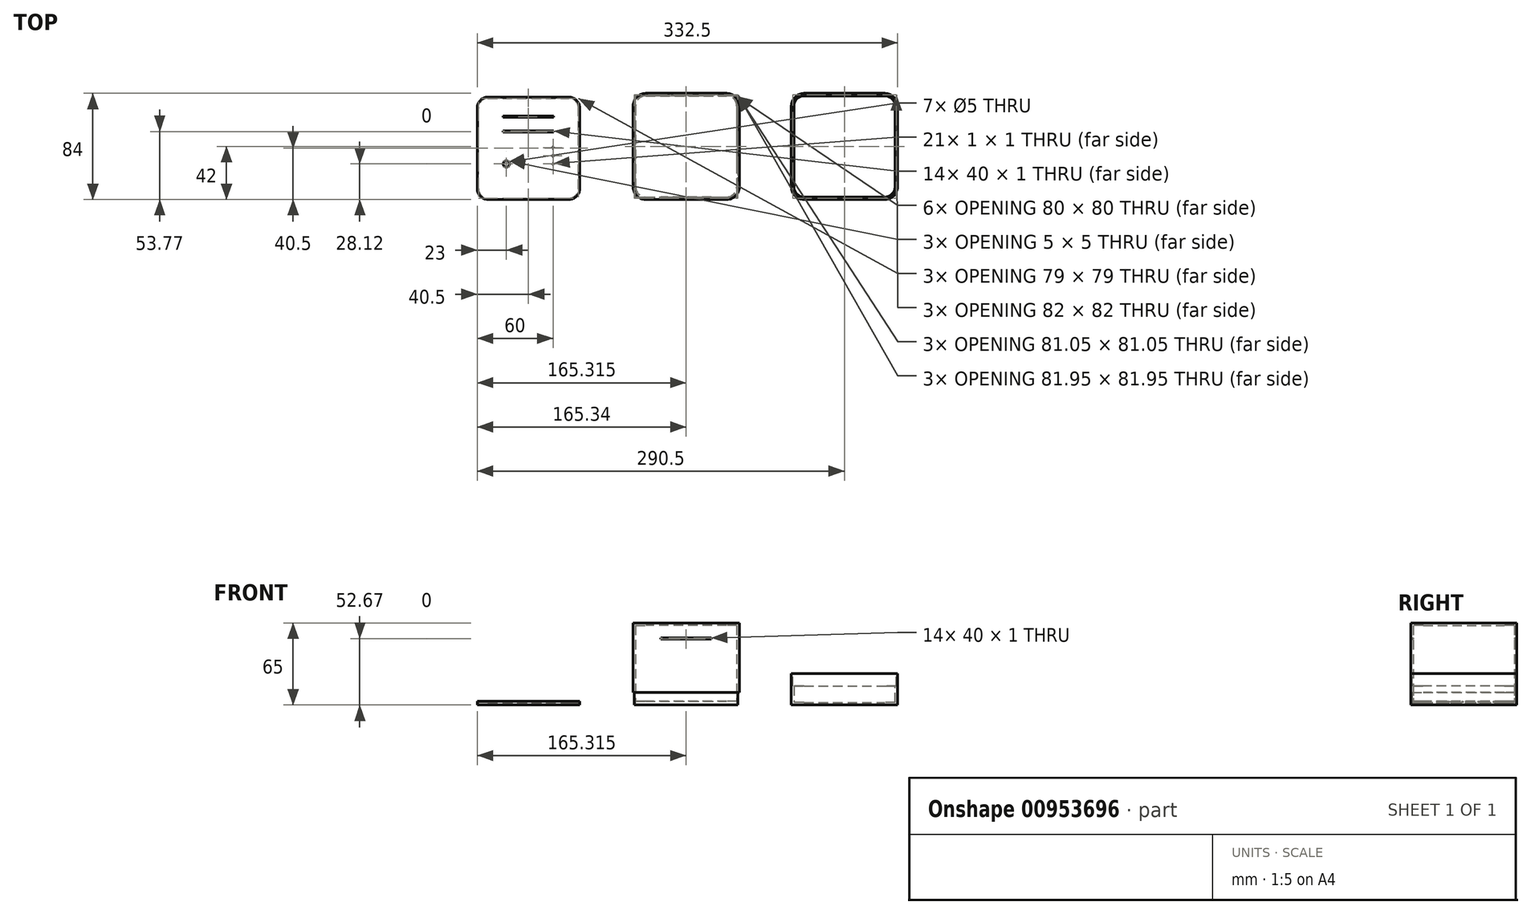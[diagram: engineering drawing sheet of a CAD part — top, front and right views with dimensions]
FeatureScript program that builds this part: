
annotation { "Feature Type Name" : "Feature", "Feature Type Description" : "" }
export const myFeature = defineFeature(function(context is Context, id is Id, definition is map)
    precondition{}
    {
        {
            var Q0;
            Q0=qCreatedBy(makeId("Top.planeOp"),FACE);
            var sketch = newSketch(context, id + "F0", { "sketchPlane" : qUnion([Q0])});
            skLineSegment(sketch, "E0.bottom", {"start": v(-32, -42) * mm, "end": v(32, -42) * mm});
            skLineSegment(sketch, "E0.top", {"start": v(-32, 42) * mm, "end": v(32, 42) * mm});
            skLineSegment(sketch, "E0.left", {"start": v(-42, -32) * mm, "end": v(-42, 32) * mm});
            skLineSegment(sketch, "E0.right", {"start": v(42, -32) * mm, "end": v(42, 32) * mm});
            skPoint(sketch, "E0.middle", {"position": v(0, 0) * mm});
            skPoint(sketch, "E1.visualSharp", {"position": v(-42, 42) * mm});
            skArc(sketch, "E1.filletArc", {"start": v(-32, 42) * mm, "mid": v(-39.07, 39.07) * mm, "end": v(-42, 32) * mm});
            skPoint(sketch, "E2.visualSharp", {"position": v(42, 42) * mm});
            skArc(sketch, "E2.filletArc", {"start": v(42, 32) * mm, "mid": v(39.07, 39.07) * mm, "end": v(32, 42) * mm});
            skPoint(sketch, "E3.visualSharp", {"position": v(42, -42) * mm});
            skArc(sketch, "E3.filletArc", {"start": v(32, -42) * mm, "mid": v(39.07, -39.07) * mm, "end": v(42, -32) * mm});
            skPoint(sketch, "E4.visualSharp", {"position": v(-42, -42) * mm});
            skArc(sketch, "E4.filletArc", {"start": v(-42, -32) * mm, "mid": v(-39.07, -39.07) * mm, "end": v(-32, -42) * mm});
            skSolve(sketch);
        }
        {
            var Q0;
            Q0 = qSketchRegion(id + "F0", true);
            extrude(context, id + "F1", {"entities" : qUnion([Q0]), "depth" : 25 * mm, "offsetDistance" : 25 * mm});
        }
        {
            var Q0;
            Q0=makeQuery(id+"F1.opExtrude","CAP_FACE",FACE,{"disambiguationData":[OSD([sQuery(id+"F0.wireOp",EDGE,"E0.bottom"),sQuery(id+"F0.wireOp",EDGE,"E0.top"),sQuery(id+"F0.wireOp",EDGE,"E0.left"),sQuery(id+"F0.wireOp",EDGE,"E0.right"),sQuery(id+"F0.wireOp",EDGE,"E1.filletArc"),sQuery(id+"F0.wireOp",EDGE,"E2.filletArc"),sQuery(id+"F0.wireOp",EDGE,"E3.filletArc"),sQuery(id+"F0.wireOp",EDGE,"E4.filletArc")])],"isStart":false});
            shell(context, id + "F2", {"entities" : qUnion([Q0]), "thickness" : 2 * mm});
        }
        {
            var Q0;
            Q0=makeQuery(id+"F1.opExtrude","CAP_FACE",FACE,{"disambiguationData":[OSD([sQuery(id+"F0.wireOp",EDGE,"E0.bottom"),sQuery(id+"F0.wireOp",EDGE,"E0.top"),sQuery(id+"F0.wireOp",EDGE,"E0.left"),sQuery(id+"F0.wireOp",EDGE,"E0.right"),sQuery(id+"F0.wireOp",EDGE,"E1.filletArc"),sQuery(id+"F0.wireOp",EDGE,"E2.filletArc"),sQuery(id+"F0.wireOp",EDGE,"E3.filletArc"),sQuery(id+"F0.wireOp",EDGE,"E4.filletArc")])],"isStart":false});
            var sketch = newSketch(context, id + "F3", { "sketchPlane" : qUnion([Q0])});
            skLineSegment(sketch, "E5.bottom", {"start": v(-32, 41) * mm, "end": v(32, 41) * mm});
            skLineSegment(sketch, "E5.top", {"start": v(-32, -41) * mm, "end": v(32, -41) * mm});
            skLineSegment(sketch, "E5.left", {"start": v(-41, 32) * mm, "end": v(-41, -32) * mm});
            skLineSegment(sketch, "E5.right", {"start": v(41, 32) * mm, "end": v(41, -32) * mm});
            skPoint(sketch, "E5.middle", {"position": v(0, 0) * mm});
            skPoint(sketch, "E6.visualSharp", {"position": v(-41, 41) * mm});
            skArc(sketch, "E6.filletArc", {"start": v(-32, 41) * mm, "mid": v(-38.36, 38.36) * mm, "end": v(-41, 32) * mm});
            skPoint(sketch, "E7.visualSharp", {"position": v(41, 41) * mm});
            skArc(sketch, "E7.filletArc", {"start": v(41, 32) * mm, "mid": v(38.36, 38.36) * mm, "end": v(32, 41) * mm});
            skPoint(sketch, "E8.visualSharp", {"position": v(41, -41) * mm});
            skArc(sketch, "E8.filletArc", {"start": v(32, -41) * mm, "mid": v(38.36, -38.36) * mm, "end": v(41, -32) * mm});
            skPoint(sketch, "E9.visualSharp", {"position": v(-41, -41) * mm});
            skArc(sketch, "E9.filletArc", {"start": v(-41, -32) * mm, "mid": v(-38.36, -38.36) * mm, "end": v(-32, -41) * mm});
            skSolve(sketch);
        }
        {
            var Q0;
            Q0 = qSketchRegion(id + "F3", true);
            extrude(context, id + "F4", {"entities" : qUnion([Q0]), "operationType" : NewBodyOperationType.REMOVE, "oppositeDirection" : true, "depth" : 10 * mm, "offsetDistance" : 25 * mm});
        }
        {
            var Q0;
            Q0=qCreatedBy(makeId("Top.planeOp"),FACE);
            var sketch = newSketch(context, id + "F5", { "sketchPlane" : qUnion([Q0])});
            skLineSegment(sketch, "E10.bottom", {"start": v(-93.19, -42) * mm, "end": v(-157.19, -42) * mm});
            skLineSegment(sketch, "E10.top", {"start": v(-93.19, 42) * mm, "end": v(-157.19, 42) * mm});
            skLineSegment(sketch, "E10.left", {"start": v(-83.19, -32) * mm, "end": v(-83.19, 32) * mm});
            skLineSegment(sketch, "E10.right", {"start": v(-167.19, -32) * mm, "end": v(-167.19, 32) * mm});
            skPoint(sketch, "E10.middle", {"position": v(-125.19, 0) * mm});
            skPoint(sketch, "E11.visualSharp", {"position": v(-167.19, -42) * mm});
            skArc(sketch, "E11.filletArc", {"start": v(-167.19, -32) * mm, "mid": v(-164.26, -39.07) * mm, "end": v(-157.19, -42) * mm});
            skPoint(sketch, "E12.visualSharp", {"position": v(-83.19, -42) * mm});
            skArc(sketch, "E12.filletArc", {"start": v(-93.19, -42) * mm, "mid": v(-86.11, -39.07) * mm, "end": v(-83.19, -32) * mm});
            skPoint(sketch, "E13.visualSharp", {"position": v(-83.19, 42) * mm});
            skArc(sketch, "E13.filletArc", {"start": v(-83.19, 32) * mm, "mid": v(-86.11, 39.07) * mm, "end": v(-93.19, 42) * mm});
            skPoint(sketch, "E14.visualSharp", {"position": v(-167.19, 42) * mm});
            skArc(sketch, "E14.filletArc", {"start": v(-157.19, 42) * mm, "mid": v(-164.26, 39.07) * mm, "end": v(-167.19, 32) * mm});
            skSolve(sketch);
        }
        {
            var Q0;
            Q0 = qSketchRegion(id + "F5", true);
            extrude(context, id + "F6", {"entities" : qUnion([Q0]), "depth" : 65 * mm, "offsetDistance" : 25 * mm});
        }
        {
            var Q0;
            Q0=makeQuery(id+"F6.opExtrude","CAP_FACE",FACE,{"disambiguationData":[OSD([sQuery(id+"F5.wireOp",EDGE,"E10.bottom"),sQuery(id+"F5.wireOp",EDGE,"E10.top"),sQuery(id+"F5.wireOp",EDGE,"E10.left"),sQuery(id+"F5.wireOp",EDGE,"E10.right"),sQuery(id+"F5.wireOp",EDGE,"E11.filletArc"),sQuery(id+"F5.wireOp",EDGE,"E12.filletArc"),sQuery(id+"F5.wireOp",EDGE,"E13.filletArc"),sQuery(id+"F5.wireOp",EDGE,"E14.filletArc")])],"isStart":true});
            shell(context, id + "F7", {"entities" : qUnion([Q0]), "thickness" : 2 * mm});
        }
        {
            var Q0;
            Q0=makeQuery(id+"F6.opExtrude","CAP_FACE",FACE,{"disambiguationData":[OSD([sQuery(id+"F5.wireOp",EDGE,"E10.bottom"),sQuery(id+"F5.wireOp",EDGE,"E10.top"),sQuery(id+"F5.wireOp",EDGE,"E10.left"),sQuery(id+"F5.wireOp",EDGE,"E10.right"),sQuery(id+"F5.wireOp",EDGE,"E11.filletArc"),sQuery(id+"F5.wireOp",EDGE,"E12.filletArc"),sQuery(id+"F5.wireOp",EDGE,"E13.filletArc"),sQuery(id+"F5.wireOp",EDGE,"E14.filletArc")])],"isStart":true});
            var sketch = newSketch(context, id + "F8", { "sketchPlane" : qUnion([Q0])});
            skLineSegment(sketch, "E15.bottom", {"start": v(-157.16, 40.97) * mm, "end": v(-93.21, 40.97) * mm});
            skLineSegment(sketch, "E15.top", {"start": v(-157.16, -40.98) * mm, "end": v(-93.21, -40.98) * mm});
            skLineSegment(sketch, "E15.left", {"start": v(-166.16, 31.97) * mm, "end": v(-166.16, -31.98) * mm});
            skLineSegment(sketch, "E15.right", {"start": v(-84.21, 31.97) * mm, "end": v(-84.21, -31.98) * mm});
            skPoint(sketch, "E15.middle", {"position": v(-125.19, 0) * mm});
            skPoint(sketch, "E15.middle.positionSnap0", {"position": v(-85.19, 0) * mm});
            skPoint(sketch, "E15.centerSnap0", {"position": v(-85.19, 0) * mm});
            skPoint(sketch, "E16.visualSharp", {"position": v(-166.16, -40.98) * mm});
            skArc(sketch, "E16.filletArc", {"start": v(-166.16, -31.98) * mm, "mid": v(-163.52, -38.34) * mm, "end": v(-157.16, -40.98) * mm});
            skPoint(sketch, "E17.visualSharp", {"position": v(-84.21, -40.98) * mm});
            skArc(sketch, "E17.filletArc", {"start": v(-93.21, -40.98) * mm, "mid": v(-86.85, -38.34) * mm, "end": v(-84.21, -31.98) * mm});
            skPoint(sketch, "E18.visualSharp", {"position": v(-84.21, 40.97) * mm});
            skArc(sketch, "E18.filletArc", {"start": v(-84.21, 31.97) * mm, "mid": v(-86.85, 38.34) * mm, "end": v(-93.21, 40.97) * mm});
            skPoint(sketch, "E19.visualSharp", {"position": v(-166.16, 40.97) * mm});
            skArc(sketch, "E19.filletArc", {"start": v(-157.16, 40.97) * mm, "mid": v(-163.52, 38.34) * mm, "end": v(-166.16, 31.97) * mm});
            skLineSegment(sketch, "E20.bottom", {"start": v(-170.77, -49.26) * mm, "end": v(-79.6, -49.26) * mm});
            skLineSegment(sketch, "E20.top", {"start": v(-170.77, 49.26) * mm, "end": v(-79.6, 49.26) * mm});
            skLineSegment(sketch, "E20.left", {"start": v(-170.77, -49.26) * mm, "end": v(-170.77, 49.26) * mm});
            skLineSegment(sketch, "E20.right", {"start": v(-79.6, -49.26) * mm, "end": v(-79.6, 49.26) * mm});
            skSolve(sketch);
        }
        {
            var Q0;
            Q0 = qSketchRegion(id + "F8", true);
            extrude(context, id + "F9", {"entities" : qUnion([Q0]), "operationType" : NewBodyOperationType.REMOVE, "oppositeDirection" : true, "depth" : 10 * mm, "offsetDistance" : 25 * mm});
        }
        {
            var Q0;
            Q0=makeQuery(id+"F6.opExtrude","CAP_FACE",FACE,{"disambiguationData":[OSD([sQuery(id+"F5.wireOp",EDGE,"E10.bottom"),sQuery(id+"F5.wireOp",EDGE,"E10.top"),sQuery(id+"F5.wireOp",EDGE,"E10.left"),sQuery(id+"F5.wireOp",EDGE,"E10.right"),sQuery(id+"F5.wireOp",EDGE,"E11.filletArc"),sQuery(id+"F5.wireOp",EDGE,"E12.filletArc"),sQuery(id+"F5.wireOp",EDGE,"E13.filletArc"),sQuery(id+"F5.wireOp",EDGE,"E14.filletArc")])],"isStart":true});
            var sketch = newSketch(context, id + "F10", { "sketchPlane" : qUnion([Q0])});
            skLineSegment(sketch, "E21.bottom", {"start": v(-93.14, -40.52) * mm, "end": v(-157.19, -40.52) * mm});
            skLineSegment(sketch, "E21.top", {"start": v(-93.14, 40.53) * mm, "end": v(-157.19, 40.53) * mm});
            skLineSegment(sketch, "E21.left", {"start": v(-84.64, -32.02) * mm, "end": v(-84.64, 32.03) * mm});
            skLineSegment(sketch, "E21.right", {"start": v(-165.69, -32.02) * mm, "end": v(-165.69, 32.03) * mm});
            skPoint(sketch, "E21.middle", {"position": v(-125.19, 0) * mm});
            skPoint(sketch, "E21.middle.positionSnap0", {"position": v(-125.19, 40) * mm});
            skPoint(sketch, "E21.centerSnap0", {"position": v(-125.19, 40) * mm});
            skPoint(sketch, "E22.newPointB", {"position": v(-165.74, 40.53) * mm});
            skArc(sketch, "E22.filletArc", {"start": v(-157.19, 40.53) * mm, "mid": v(-163.2, 38.04) * mm, "end": v(-165.69, 32.03) * mm});
            skPoint(sketch, "E23.newPointB", {"position": v(-84.69, 40.53) * mm});
            skArc(sketch, "E23.filletArc", {"start": v(-84.64, 32.03) * mm, "mid": v(-87.12, 38.04) * mm, "end": v(-93.14, 40.53) * mm});
            skPoint(sketch, "E24.visualSharp", {"position": v(-84.64, -40.52) * mm});
            skArc(sketch, "E24.filletArc", {"start": v(-93.14, -40.53) * mm, "mid": v(-87.12, -38.04) * mm, "end": v(-84.64, -32.02) * mm});
            skPoint(sketch, "E25.visualSharp", {"position": v(-165.69, -40.52) * mm});
            skArc(sketch, "E25.filletArc", {"start": v(-165.69, -32.02) * mm, "mid": v(-163.2, -38.04) * mm, "end": v(-157.19, -40.53) * mm});
            skSolve(sketch);
        }
        {
            var Q0;
            Q0 = qSketchRegion(id + "F10", true);
            extrude(context, id + "F11", {"entities" : qUnion([Q0]), "operationType" : NewBodyOperationType.REMOVE, "oppositeDirection" : true, "depth" : 3 * mm, "offsetDistance" : 25 * mm});
        }
        {
            var Q0;
            Q0=qCreatedBy(makeId("Top.planeOp"),FACE);
            var sketch = newSketch(context, id + "F12", { "sketchPlane" : qUnion([Q0])});
            skLineSegment(sketch, "E26.bottom", {"start": v(-282, -42) * mm, "end": v(-218, -42) * mm});
            skLineSegment(sketch, "E26.top", {"start": v(-282, 39) * mm, "end": v(-218, 39) * mm});
            skLineSegment(sketch, "E26.left", {"start": v(-290.5, -33.5) * mm, "end": v(-290.5, 30.5) * mm});
            skLineSegment(sketch, "E26.right", {"start": v(-209.5, -33.5) * mm, "end": v(-209.5, 30.5) * mm});
            skPoint(sketch, "E26.middle", {"position": v(-250, -1.5) * mm});
            skPoint(sketch, "E27.visualSharp", {"position": v(-290.5, -42) * mm});
            skArc(sketch, "E27.filletArc", {"start": v(-290.5, -33.5) * mm, "mid": v(-288.01, -39.51) * mm, "end": v(-282, -42) * mm});
            skPoint(sketch, "E28.visualSharp", {"position": v(-209.5, -42) * mm});
            skArc(sketch, "E28.filletArc", {"start": v(-218, -42) * mm, "mid": v(-211.99, -39.51) * mm, "end": v(-209.5, -33.5) * mm});
            skPoint(sketch, "E29.visualSharp", {"position": v(-209.5, 39) * mm});
            skArc(sketch, "E29.filletArc", {"start": v(-209.5, 30.5) * mm, "mid": v(-211.99, 36.51) * mm, "end": v(-218, 39) * mm});
            skPoint(sketch, "E30.visualSharp", {"position": v(-290.5, 39) * mm});
            skArc(sketch, "E30.filletArc", {"start": v(-282, 39) * mm, "mid": v(-288.01, 36.51) * mm, "end": v(-290.5, 30.5) * mm});
            skLineSegment(sketch, "E31.bottom", {"start": v(-230, 24.03) * mm, "end": v(-270, 24.03) * mm});
            skLineSegment(sketch, "E31.top", {"start": v(-230, 23.03) * mm, "end": v(-270, 23.03) * mm});
            skLineSegment(sketch, "E31.left", {"start": v(-230, 23.03) * mm, "end": v(-230, 24.03) * mm});
            skLineSegment(sketch, "E31.right", {"start": v(-270, 23.03) * mm, "end": v(-270, 24.03) * mm});
            skPoint(sketch, "E31.middle", {"position": v(-250, 23.53) * mm});
            skLineSegment(sketch, "E32.bottom", {"start": v(-230, 11.27) * mm, "end": v(-270, 11.27) * mm});
            skLineSegment(sketch, "E32.top", {"start": v(-230, 12.27) * mm, "end": v(-270, 12.27) * mm});
            skLineSegment(sketch, "E32.left", {"start": v(-230, 11.27) * mm, "end": v(-230, 12.27) * mm});
            skLineSegment(sketch, "E32.right", {"start": v(-270, 11.27) * mm, "end": v(-270, 12.27) * mm});
            skPoint(sketch, "E32.middle", {"position": v(-250, 11.77) * mm});
            skLineSegment(sketch, "E33.bottom", {"start": v(-230, -13.38) * mm, "end": v(-231, -13.38) * mm});
            skLineSegment(sketch, "E33.top", {"start": v(-230, -14.38) * mm, "end": v(-231, -14.38) * mm});
            skLineSegment(sketch, "E33.left", {"start": v(-230, -13.38) * mm, "end": v(-230, -14.38) * mm});
            skLineSegment(sketch, "E33.right", {"start": v(-231, -13.38) * mm, "end": v(-231, -14.38) * mm});
            skPoint(sketch, "E33.middle", {"position": v(-230.5, -13.88) * mm});
            skLineSegment(sketch, "E34.bottom", {"start": v(-230, -7.95) * mm, "end": v(-231, -7.95) * mm});
            skLineSegment(sketch, "E34.top", {"start": v(-230, -6.95) * mm, "end": v(-231, -6.95) * mm});
            skLineSegment(sketch, "E34.left", {"start": v(-230, -7.95) * mm, "end": v(-230, -6.95) * mm});
            skLineSegment(sketch, "E34.right", {"start": v(-231, -7.95) * mm, "end": v(-231, -6.95) * mm});
            skPoint(sketch, "E34.middle", {"position": v(-230.5, -7.45) * mm});
            skLineSegment(sketch, "E35.bottom", {"start": v(-230, -1.52) * mm, "end": v(-231, -1.52) * mm});
            skLineSegment(sketch, "E35.top", {"start": v(-230, -0.52) * mm, "end": v(-231, -0.52) * mm});
            skLineSegment(sketch, "E35.left", {"start": v(-230, -1.52) * mm, "end": v(-230, -0.52) * mm});
            skLineSegment(sketch, "E35.right", {"start": v(-231, -1.52) * mm, "end": v(-231, -0.52) * mm});
            skPoint(sketch, "E35.middle", {"position": v(-230.5, -1.02) * mm});
            skCircle(sketch, "E36", {"center": v(-267.5, -13.88) * mm, "radius": 2.5 * mm});
            skSolve(sketch);
        }
        {
            var Q0;
            Q0 = qSketchRegion(id + "F12", true);
            extrude(context, id + "F13", {"entities" : qUnion([Q0]), "depth" : 3 * mm, "offsetDistance" : 25 * mm});
        }
        {
            var Q0;
            Q0=makeQuery(id+"F6.opExtrude","SWEPT_FACE",FACE,{"disambiguationData":[OSD([sQuery(id+"F5.wireOp",EDGE,"E10.top")])]});
            var sketch = newSketch(context, id + "F14", { "sketchPlane" : qUnion([Q0])});
            skLineSegment(sketch, "E37.bottom", {"start": v(145.19, 52.17) * mm, "end": v(105.19, 52.17) * mm});
            skLineSegment(sketch, "E37.top", {"start": v(145.19, 53.17) * mm, "end": v(105.19, 53.17) * mm});
            skLineSegment(sketch, "E37.left", {"start": v(145.19, 52.17) * mm, "end": v(145.19, 53.17) * mm});
            skLineSegment(sketch, "E37.right", {"start": v(105.19, 52.17) * mm, "end": v(105.19, 53.17) * mm});
            skPoint(sketch, "E37.middle", {"position": v(125.19, 52.67) * mm});
            skSolve(sketch);
        }
        {
            var Q0;
            Q0 = qSketchRegion(id + "F14", true);
            extrude(context, id + "F15", {"entities" : qUnion([Q0]), "operationType" : NewBodyOperationType.REMOVE, "endBound" : BoundingType.THROUGH_ALL, "oppositeDirection" : true, "depth" : 25 * mm, "offsetDistance" : 25 * mm});
        }
        {
            var Q0;
            Q0=makeQuery(id+"F13.opExtrude","CAP_FACE",FACE,{"disambiguationData":[OSD([sQuery(id+"F12.wireOp",EDGE,"E26.bottom"),sQuery(id+"F12.wireOp",EDGE,"E26.top"),sQuery(id+"F12.wireOp",EDGE,"E26.left"),sQuery(id+"F12.wireOp",EDGE,"E26.right"),sQuery(id+"F12.wireOp",EDGE,"E27.filletArc"),sQuery(id+"F12.wireOp",EDGE,"E28.filletArc"),sQuery(id+"F12.wireOp",EDGE,"E29.filletArc"),sQuery(id+"F12.wireOp",EDGE,"E30.filletArc"),sQuery(id+"F12.wireOp",EDGE,"E31.bottom"),sQuery(id+"F12.wireOp",EDGE,"E31.top"),sQuery(id+"F12.wireOp",EDGE,"E31.left"),sQuery(id+"F12.wireOp",EDGE,"E31.right"),sQuery(id+"F12.wireOp",EDGE,"E32.bottom"),sQuery(id+"F12.wireOp",EDGE,"E32.top"),sQuery(id+"F12.wireOp",EDGE,"E32.left"),sQuery(id+"F12.wireOp",EDGE,"E32.right"),sQuery(id+"F12.wireOp",EDGE,"E33.bottom"),sQuery(id+"F12.wireOp",EDGE,"E33.top"),sQuery(id+"F12.wireOp",EDGE,"E33.left"),sQuery(id+"F12.wireOp",EDGE,"E33.right"),sQuery(id+"F12.wireOp",EDGE,"E34.bottom"),sQuery(id+"F12.wireOp",EDGE,"E34.top"),sQuery(id+"F12.wireOp",EDGE,"E34.left"),sQuery(id+"F12.wireOp",EDGE,"E34.right"),sQuery(id+"F12.wireOp",EDGE,"E35.bottom"),sQuery(id+"F12.wireOp",EDGE,"E35.top"),sQuery(id+"F12.wireOp",EDGE,"E35.left"),sQuery(id+"F12.wireOp",EDGE,"E35.right"),sQuery(id+"F12.wireOp",EDGE,"E36")])],"isStart":true});
            shell(context, id + "F16", {"entities" : qUnion([Q0]), "thickness" : 1 * mm});
        }
        {
            var Q0;
            {var subQ0=sQuery(id+"F12.wireOp",EDGE,"E36");var subQ1=sQuery(id+"F12.wireOp",EDGE,"E35.right");var subQ2=sQuery(id+"F12.wireOp",EDGE,"E35.left");var subQ3=sQuery(id+"F12.wireOp",EDGE,"E35.top");var subQ4=sQuery(id+"F12.wireOp",EDGE,"E35.bottom");var subQ5=sQuery(id+"F12.wireOp",EDGE,"E34.right");var subQ6=sQuery(id+"F12.wireOp",EDGE,"E34.left");var subQ7=sQuery(id+"F12.wireOp",EDGE,"E34.top");var subQ8=sQuery(id+"F12.wireOp",EDGE,"E34.bottom");var subQ9=sQuery(id+"F12.wireOp",EDGE,"E33.right");var subQ10=sQuery(id+"F12.wireOp",EDGE,"E33.left");var subQ11=sQuery(id+"F12.wireOp",EDGE,"E33.top");var subQ12=sQuery(id+"F12.wireOp",EDGE,"E33.bottom");var subQ13=sQuery(id+"F12.wireOp",EDGE,"E32.right");var subQ14=sQuery(id+"F12.wireOp",EDGE,"E32.left");var subQ15=sQuery(id+"F12.wireOp",EDGE,"E32.top");var subQ16=sQuery(id+"F12.wireOp",EDGE,"E32.bottom");var subQ17=sQuery(id+"F12.wireOp",EDGE,"E31.right");var subQ18=sQuery(id+"F12.wireOp",EDGE,"E31.left");var subQ19=sQuery(id+"F12.wireOp",EDGE,"E31.top");var subQ20=sQuery(id+"F12.wireOp",EDGE,"E31.bottom");var subQ21=sQuery(id+"F12.wireOp",EDGE,"E30.filletArc");var subQ22=sQuery(id+"F12.wireOp",EDGE,"E29.filletArc");var subQ23=sQuery(id+"F12.wireOp",EDGE,"E28.filletArc");var subQ24=sQuery(id+"F12.wireOp",EDGE,"E27.filletArc");var subQ25=sQuery(id+"F12.wireOp",EDGE,"E26.right");var subQ26=sQuery(id+"F12.wireOp",EDGE,"E26.left");var subQ27=sQuery(id+"F12.wireOp",EDGE,"E26.top");var subQ28=sQuery(id+"F12.wireOp",EDGE,"E26.bottom");Q0=makeQuery(id+"F16.opShell","OFFSET_FACE",FACE,{"disambiguationData":[OSD([subQ28,subQ27,subQ26,subQ25,subQ24,subQ23,subQ22,subQ21,subQ20,subQ19,subQ18,subQ17,subQ16,subQ15,subQ14,subQ13,subQ12,subQ11,subQ10,subQ9,subQ8,subQ7,subQ6,subQ5,subQ4,subQ3,subQ2,subQ1,subQ0]),TDD([makeQuery(id+"F13.opExtrude","CAP_FACE",FACE,{"disambiguationData":[OSD([subQ28,subQ27,subQ26,subQ25,subQ24,subQ23,subQ22,subQ21,subQ20,subQ19,subQ18,subQ17,subQ16,subQ15,subQ14,subQ13,subQ12,subQ11,subQ10,subQ9,subQ8,subQ7,subQ6,subQ5,subQ4,subQ3,subQ2,subQ1,subQ0])],"isStart":false})])]});}
            var sketch = newSketch(context, id + "F17", { "sketchPlane" : qUnion([Q0])});
            skLineSegment(sketch, "E38.bottom", {"start": v(-277.37, 22.6) * mm, "end": v(-221.1, 22.6) * mm});
            skLineSegment(sketch, "E38.top", {"start": v(-277.37, -29.97) * mm, "end": v(-221.1, -29.97) * mm});
            skLineSegment(sketch, "E38.left", {"start": v(-277.37, 22.6) * mm, "end": v(-277.37, -29.97) * mm});
            skLineSegment(sketch, "E38.right", {"start": v(-221.1, 22.6) * mm, "end": v(-221.1, -29.97) * mm});
            skSolve(sketch);
        }
        {
            var Q0;
            Q0 = qSketchRegion(id + "F17", true);
            extrude(context, id + "F18", {"entities" : qUnion([Q0]), "operationType" : NewBodyOperationType.REMOVE, "depth" : 25 * mm, "offsetDistance" : 25 * mm});
        }
    });
